# Revit family: Shower-Valve_Trim-KALLISTA-Italy-P33363
name_source: partatom
category: Specialty Equipment
units: mm (PartAtom-declared; Revit-internal decimal feet)

## family parameters
Cut with Voids When Loaded = No
Host = Face
OmniClass Number = 23.31.25.00
OmniClass Title = Toilet and Bath Specialties
Part Type = Normal
Room Calculation Point = No
Round Connector Dimension = Use Diameter
Shared = No

## types (6) — shared parameters
ADA Compliant = No
Assembly Code = C1030200
Date Modified = 10/18/2024
Default Elevation = 42"
Description = 1-Outlet Stacked Thermostatic Trim With Diverter
Handle Clearance = 1 9/16"
Height = 7 7/8"
Length = 4"
Manufacturer = Kallista Co.
Master Format 2014 = 10 28 00
Master Format 2014 Name = Toilet, Bath, and Laundry Accessories
Material = Premium Metal Construction
Product Name = Italy
URL = https://www.kallista.com
WaterSense Certified = No
Width = 4 9/16"

## per-type parameters (varying)
| type | Finish | Model | Type |
| 2MB-Brushed Brass | Kallista-Metal-2MB- Brushed_Brass | P33363-00-2MB | 1 |
| BGP-Brushed Graphite | Kallista-Metal-BGP-Brushed_Graphite | P33363-00-BGP | 2 |
| BLH-Blush Brass | Kallista-Metal-BLH-Blush_Brass | P33363-00-BLH | 3 |
| BN-Brushed Nickel | Kallista-Metal-BN-Brushed_Nickel | P33363-00-BN | 4 |
| CP-Chrome | Kallista-Metal-CP-Chrome | P33363-00-CP | 5 |
| PGP-Polished Graphite | Kallista-Metal-PGP-Polished_Graphite | P33363-00-PGP | 6 |

## geometry (parser evidence)
native form markers: Sweep x5
no freeform markers — native parametric forms only
